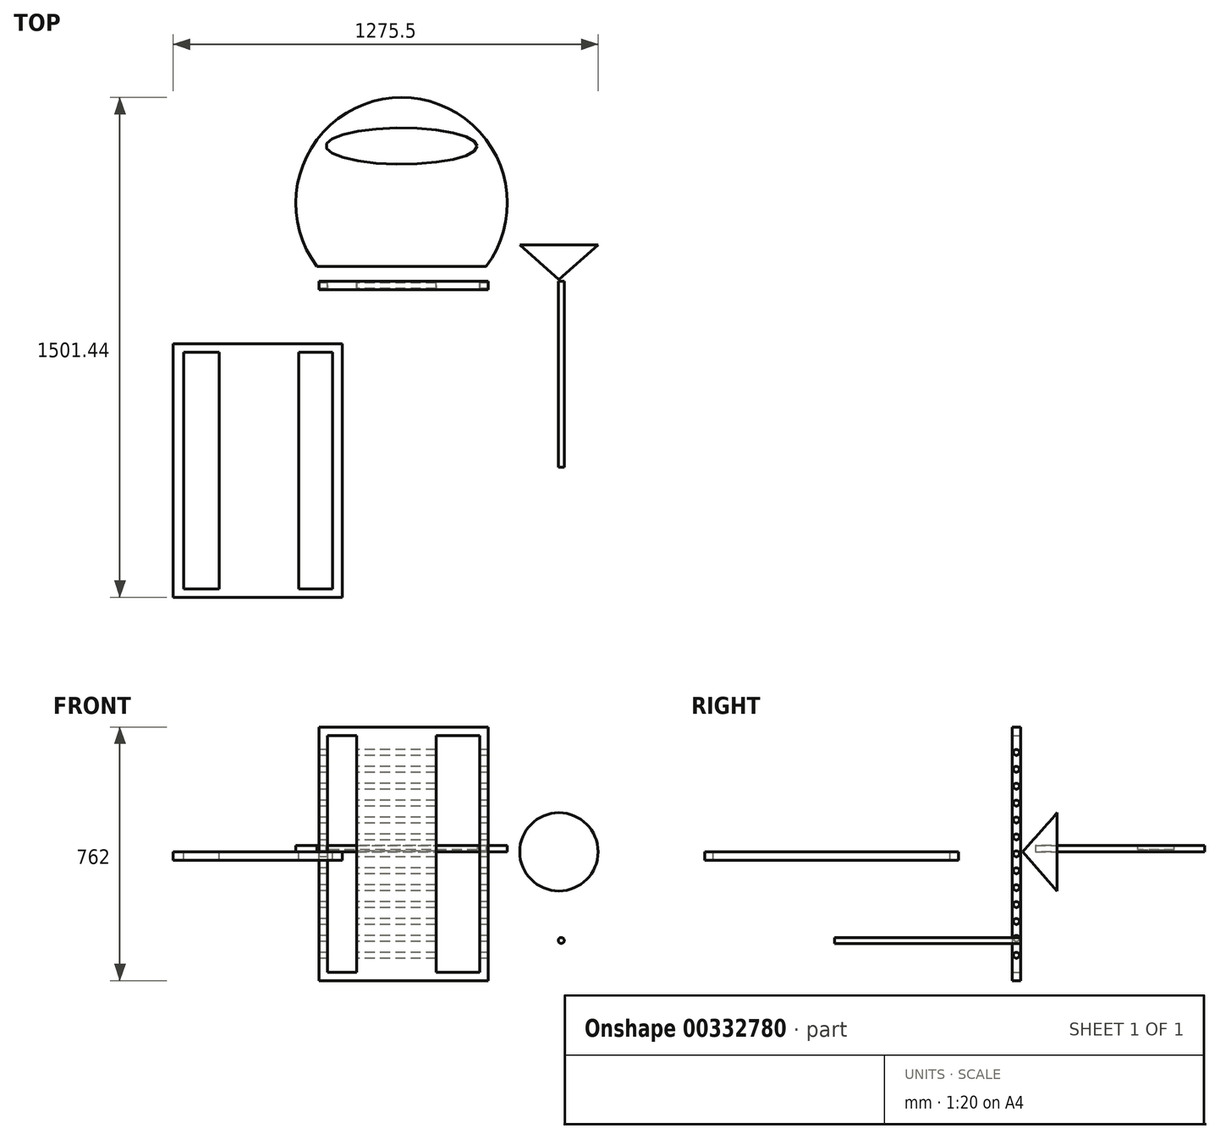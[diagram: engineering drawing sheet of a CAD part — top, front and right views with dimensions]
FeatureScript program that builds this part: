
annotation { "Feature Type Name" : "Feature", "Feature Type Description" : "" }
export const myFeature = defineFeature(function(context is Context, id is Id, definition is map)
    precondition{}
    {
        {
            var Q0;
            Q0=qCreatedBy(makeId("Front.planeOp"),FACE);
            var sketch = newSketch(context, id + "F0", { "sketchPlane" : qUnion([Q0])});
            skLineSegment(sketch, "E0", {"start": v(-402.52, -386.82) * mm, "end": v(-402.52, 375.18) * mm});
            skLineSegment(sketch, "E1", {"start": v(-402.52, 375.18) * mm, "end": v(105.48, 375.18) * mm});
            skLineSegment(sketch, "E2", {"start": v(105.48, 375.18) * mm, "end": v(105.48, -386.82) * mm});
            skLineSegment(sketch, "E3", {"start": v(105.48, -386.82) * mm, "end": v(-402.52, -386.82) * mm});
            skLineSegment(sketch, "E4", {"start": v(80.05, 349.78) * mm, "end": v(-51.74, 349.78) * mm});
            skLineSegment(sketch, "E5", {"start": v(-51.74, 349.78) * mm, "end": v(-51.74, -361.42) * mm});
            skLineSegment(sketch, "E6", {"start": v(-51.74, -361.42) * mm, "end": v(80.05, -361.42) * mm});
            skLineSegment(sketch, "E7", {"start": v(80.05, -361.42) * mm, "end": v(80.05, 349.78) * mm});
            skLineSegment(sketch, "E8", {"start": v(-51.74, 349.78) * mm, "end": v(-51.74, 375.18) * mm});
            skLineSegment(sketch, "E9", {"start": v(80.05, -361.42) * mm, "end": v(80.05, -386.82) * mm});
            skLineSegment(sketch, "E10", {"start": v(-290, 349.78) * mm, "end": v(-378.17, 349.78) * mm});
            skLineSegment(sketch, "E11", {"start": v(-378.17, 349.78) * mm, "end": v(-378.17, -361.42) * mm});
            skLineSegment(sketch, "E12", {"start": v(-378.17, -361.42) * mm, "end": v(-290, -361.42) * mm});
            skLineSegment(sketch, "E13", {"start": v(-290, -361.42) * mm, "end": v(-290, 349.78) * mm});
            skLineSegment(sketch, "E14", {"start": v(-290, -361.42) * mm, "end": v(-51.74, -361.42) * mm});
            skSolve(sketch);
        }
        {
            var Q0;
            Q0 = qSketchRegion(id + "F0", true);
            extrude(context, id + "F1", {"entities" : qUnion([Q0]), "depth" : 25.4 * mm});
        }
        {
            var Q0;
            Q0=qCreatedBy(makeId("Top.planeOp"),FACE);
            var sketch = newSketch(context, id + "F2", { "sketchPlane" : qUnion([Q0])});
            skLineSegment(sketch, "E15", {"start": v(-409.2, 44.16) * mm, "end": v(98.8, 44.16) * mm});
            skArc(sketch, "E16", {"start": v(98.8, 44.16) * mm, "mid": v(-155.2, 552.16) * mm, "end": v(-409.2, 44.16) * mm});
            skLineSegment(sketch, "E17", {"start": v(-155.2, 44.16) * mm, "end": v(-155.2, 552.16) * mm});
            skEllipse(sketch, "E18", {"center": v(-155.2, 406.06) * mm, "majorRadius": 226.76 * mm, "minorRadius": 54.56 * mm, "majorAxis": v(1, 0)});
            skSolve(sketch);
        }
        {
            var Q0;
            Q0 = qSketchRegion(id + "F2", true);
            extrude(context, id + "F3", {"entities" : qUnion([Q0]), "depth" : 19.05 * mm});
        }
        {
            var Q0;
            Q0=makeQuery(id+"F1.opExtrude","SWEPT_FACE",FACE,{"disambiguationData":[OSD([sQuery(id+"F0.wireOp",EDGE,"E0")])]});
            var sketch = newSketch(context, id + "F4", { "sketchPlane" : qUnion([Q0])});
            skCircle(sketch, "E19", {"center": v(13.05, -209.02) * mm, "radius": 8.9 * mm});
            skCircle(sketch, "E20", {"center": v(13.05, -259.82) * mm, "radius": 8.9 * mm});
            skCircle(sketch, "E21", {"center": v(13.05, -310.62) * mm, "radius": 8.9 * mm});
            skLineSegment(sketch, "E22", {"start": v(12.7, 375.18) * mm, "end": v(12.7, 349.78) * mm});
            skCircle(sketch, "E23", {"center": v(13.05, 298.98) * mm, "radius": 8.9 * mm});
            skCircle(sketch, "E24", {"center": v(13.4, 248.18) * mm, "radius": 8.9 * mm});
            skCircle(sketch, "E25", {"center": v(13.05, 197.38) * mm, "radius": 8.9 * mm});
            skCircle(sketch, "E26", {"center": v(13.05, 146.58) * mm, "radius": 8.9 * mm});
            skCircle(sketch, "E27", {"center": v(13.05, 95.78) * mm, "radius": 8.9 * mm});
            skCircle(sketch, "E28", {"center": v(13.05, 44.98) * mm, "radius": 8.9 * mm});
            skCircle(sketch, "E29", {"center": v(13.05, -5.82) * mm, "radius": 8.9 * mm});
            skCircle(sketch, "E30", {"center": v(13.05, -56.62) * mm, "radius": 8.9 * mm});
            skCircle(sketch, "E31", {"center": v(13.05, -107.42) * mm, "radius": 8.9 * mm});
            skCircle(sketch, "E32", {"center": v(13.05, -158.22) * mm, "radius": 8.9 * mm});
            skSolve(sketch);
        }
        {
            var Q0;
            Q0=makeQuery(id+"F4.imprint","IMPRINT",FACE,{"disambiguationData":[TD([[makeQuery(id+"F4.imprint","IMPRINT",EDGE,{"derivedFrom":sQuery(id+"F4.wireOp",EDGE,"KxLmF3Gb-bGkB-ipw0-DFv5-bGDR9Zjm1ckT")}),1.0]])]});
            var Q1;
            Q1=makeQuery(id+"F4.imprint","IMPRINT",FACE,{"disambiguationData":[TD([[makeQuery(id+"F4.imprint","IMPRINT",EDGE,{"derivedFrom":sQuery(id+"F4.wireOp",EDGE,"E21")}),1.0]])]});
            var Q2;
            Q2=makeQuery(id+"F4.imprint","IMPRINT",FACE,{"disambiguationData":[TD([[makeQuery(id+"F4.imprint","IMPRINT",EDGE,{"derivedFrom":sQuery(id+"F4.wireOp",EDGE,"E20")}),1.0]])]});
            var Q3;
            Q3=makeQuery(id+"F4.imprint","IMPRINT",FACE,{"disambiguationData":[TD([[makeQuery(id+"F4.imprint","IMPRINT",EDGE,{"derivedFrom":sQuery(id+"F4.wireOp",EDGE,"E19")}),1.0]])]});
            var Q4;
            Q4=makeQuery(id+"F4.imprint","IMPRINT",FACE,{"disambiguationData":[TD([[makeQuery(id+"F4.imprint","IMPRINT",EDGE,{"derivedFrom":sQuery(id+"F4.wireOp",EDGE,"SBUI3A1f-vfDp-xBPE-MnOG-4KJ5W3Gntg9e")}),1.0]])]});
            var Q5;
            Q5=makeQuery(id+"F4.imprint","IMPRINT",FACE,{"disambiguationData":[TD([[makeQuery(id+"F4.imprint","IMPRINT",EDGE,{"derivedFrom":sQuery(id+"F4.wireOp",EDGE,"ilClZEr1-WkWB-SVEu-xgAh-d21V4UNr9qtg")}),1.0]])]});
            var Q6;
            Q6=makeQuery(id+"F4.imprint","IMPRINT",FACE,{"disambiguationData":[TD([[makeQuery(id+"F4.imprint","IMPRINT",EDGE,{"derivedFrom":sQuery(id+"F4.wireOp",EDGE,"wnZTXNVM-36Ts-yCiN-EnVW-6zEoZN5PAqgz")}),1.0]])]});
            var Q7;
            Q7=makeQuery(id+"F4.imprint","IMPRINT",FACE,{"disambiguationData":[TD([[makeQuery(id+"F4.imprint","IMPRINT",EDGE,{"derivedFrom":sQuery(id+"F4.wireOp",EDGE,"8CFQUjnE-zp7q-roIU-KdL1-6CvUVFCRa30A")}),1.0]])]});
            var Q8;
            Q8=makeQuery(id+"F4.imprint","IMPRINT",FACE,{"disambiguationData":[TD([[makeQuery(id+"F4.imprint","IMPRINT",EDGE,{"derivedFrom":sQuery(id+"F4.wireOp",EDGE,"dk1FrOmF-X76H-YBRf-a3w2-1DeCIXSDKJ0s")}),1.0]])]});
            var Q9;
            Q9=makeQuery(id+"F4.imprint","IMPRINT",FACE,{"disambiguationData":[TD([[makeQuery(id+"F4.imprint","IMPRINT",EDGE,{"derivedFrom":sQuery(id+"F4.wireOp",EDGE,"kuolFWdS-myks-ns8r-KsmL-CEO9Fm7HA733")}),1.0]])]});
            var Q10;
            Q10=makeQuery(id+"F4.imprint","IMPRINT",FACE,{"disambiguationData":[TD([[makeQuery(id+"F4.imprint","IMPRINT",EDGE,{"derivedFrom":sQuery(id+"F4.wireOp",EDGE,"JJCqWmZP-dY7G-QudE-gpbD-zNKJ9OVh3fGP")}),1.0]])]});
            var Q11;
            Q11=makeQuery(id+"F4.imprint","IMPRINT",FACE,{"disambiguationData":[TD([[makeQuery(id+"F4.imprint","IMPRINT",EDGE,{"derivedFrom":sQuery(id+"F4.wireOp",EDGE,"UWQk5Cos-suA6-4IC4-ZAEo-IQIC4gf6qBqO")}),1.0]])]});
            var Q12;
            Q12=makeQuery(id+"F4.imprint","IMPRINT",FACE,{"disambiguationData":[TD([[makeQuery(id+"F4.imprint","IMPRINT",EDGE,{"derivedFrom":sQuery(id+"F4.wireOp",EDGE,"E2on6uqV-6kPG-ftVK-5GpS-Gi3AbfQCoDi4")}),1.0]])]});
            var Q13;
            Q13=makeQuery(id+"F4.imprint","IMPRINT",FACE,{"disambiguationData":[TD([[makeQuery(id+"F4.imprint","IMPRINT",EDGE,{"derivedFrom":sQuery(id+"F4.wireOp",EDGE,"fvvu0ycN-TSmg-J3CF-A7jG-3QvBUFncVqg9")}),1.0]])]});
            var Q14;
            Q14=makeQuery(id+"F4.imprint","IMPRINT",FACE,{"disambiguationData":[TD([[makeQuery(id+"F4.imprint","IMPRINT",EDGE,{"derivedFrom":sQuery(id+"F4.wireOp",EDGE,"if6vlhrL-GMo5-v6cd-j6Fg-0aG144yE2SJh")}),1.0]])]});
            var Q15;
            Q15=makeQuery(id+"F4.imprint","IMPRINT",FACE,{"disambiguationData":[TD([[makeQuery(id+"F4.imprint","IMPRINT",EDGE,{"derivedFrom":sQuery(id+"F4.wireOp",EDGE,"E26")}),1.0]])]});
            var Q16;
            Q16=makeQuery(id+"F4.imprint","IMPRINT",FACE,{"disambiguationData":[TD([[makeQuery(id+"F4.imprint","IMPRINT",EDGE,{"derivedFrom":sQuery(id+"F4.wireOp",EDGE,"E27")}),1.0]])]});
            var Q17;
            Q17=makeQuery(id+"F4.imprint","IMPRINT",FACE,{"disambiguationData":[TD([[makeQuery(id+"F4.imprint","IMPRINT",EDGE,{"derivedFrom":sQuery(id+"F4.wireOp",EDGE,"E28")}),1.0]])]});
            var Q18;
            Q18=makeQuery(id+"F4.imprint","IMPRINT",FACE,{"disambiguationData":[TD([[makeQuery(id+"F4.imprint","IMPRINT",EDGE,{"derivedFrom":sQuery(id+"F4.wireOp",EDGE,"E29")}),1.0]])]});
            var Q19;
            Q19=makeQuery(id+"F4.imprint","IMPRINT",FACE,{"disambiguationData":[TD([[makeQuery(id+"F4.imprint","IMPRINT",EDGE,{"derivedFrom":sQuery(id+"F4.wireOp",EDGE,"E30")}),1.0]])]});
            var Q20;
            Q20=makeQuery(id+"F4.imprint","IMPRINT",FACE,{"disambiguationData":[TD([[makeQuery(id+"F4.imprint","IMPRINT",EDGE,{"derivedFrom":sQuery(id+"F4.wireOp",EDGE,"E31")}),1.0]])]});
            var Q21;
            Q21=makeQuery(id+"F4.imprint","IMPRINT",FACE,{"disambiguationData":[TD([[makeQuery(id+"F4.imprint","IMPRINT",EDGE,{"derivedFrom":sQuery(id+"F4.wireOp",EDGE,"E32")}),1.0]])]});
            var Q22;
            Q22=makeQuery(id+"F4.imprint","IMPRINT",FACE,{"disambiguationData":[TD([[makeQuery(id+"F4.imprint","IMPRINT",EDGE,{"derivedFrom":sQuery(id+"F4.wireOp",EDGE,"E23")}),1.0]])]});
            var Q23;
            Q23=makeQuery(id+"F4.imprint","IMPRINT",FACE,{"disambiguationData":[TD([[makeQuery(id+"F4.imprint","IMPRINT",EDGE,{"derivedFrom":sQuery(id+"F4.wireOp",EDGE,"E24")}),1.0]])]});
            var Q24;
            Q24=makeQuery(id+"F4.imprint","IMPRINT",FACE,{"disambiguationData":[TD([[makeQuery(id+"F4.imprint","IMPRINT",EDGE,{"derivedFrom":sQuery(id+"F4.wireOp",EDGE,"E25")}),1.0]])]});
            extrude(context, id + "F5", {"entities" : qUnion([Q0, Q1, Q2, Q3, Q4, Q5, Q6, Q7, Q8, Q9, Q10, Q11, Q12, Q13, Q14, Q15, Q16, Q17, Q18, Q19, Q20, Q21, Q22, Q23, Q24]), "operationType" : NewBodyOperationType.REMOVE, "endBound" : BoundingType.THROUGH_ALL, "oppositeDirection" : true, "depth" : 25.4 * mm});
        }
        {
            var Q0;
            Q0=qCreatedBy(makeId("Top.planeOp"),FACE);
            var sketch = newSketch(context, id + "F6", { "sketchPlane" : qUnion([Q0])});
            skLineSegment(sketch, "E33", {"start": v(199.63, 109.45) * mm, "end": v(317.2, 5.52) * mm});
            skLineSegment(sketch, "E34", {"start": v(199.63, 109.45) * mm, "end": v(317.2, 109.45) * mm});
            skLineSegment(sketch, "E35", {"start": v(317.2, 109.45) * mm, "end": v(317.2, 5.52) * mm});
            skSolve(sketch);
        }
        {
            var Q0;
            Q0=makeQuery(id+"F6.imprint","IMPRINT",FACE,{"disambiguationData":[TD([[makeQuery(id+"F6.imprint","IMPRINT",EDGE,{"derivedFrom":sQuery(id+"F6.wireOp",EDGE,"E33")}),1.0]])]});
            var Q1;
            Q1=sQuery(id+"F6.wireOp",EDGE,"E35");
            revolve(context, id + "F7", {"entities" : qUnion([Q0]), "axis" : qUnion([Q1]), "revolveType" : RevolveType.FULL});
        }
        {
            var Q0;
            Q0=qCreatedBy(makeId("Front.planeOp"),FACE);
            var sketch = newSketch(context, id + "F8", { "sketchPlane" : qUnion([Q0])});
            skCircle(sketch, "E36", {"center": v(324.3, -266.21) * mm, "radius": 8.9 * mm});
            skSolve(sketch);
        }
        {
            var Q0;
            Q0=makeQuery(id+"F8.imprint","IMPRINT",FACE,{"disambiguationData":[TD([[makeQuery(id+"F8.imprint","IMPRINT",EDGE,{"derivedFrom":sQuery(id+"F8.wireOp",EDGE,"E36")}),1.0]])]});
            extrude(context, id + "F9", {"entities" : qUnion([Q0]), "depth" : 558.8 * mm});
        }
        {
            var Q0;
            Q0=qCreatedBy(makeId("Top.planeOp"),FACE);
            var sketch = newSketch(context, id + "F10", { "sketchPlane" : qUnion([Q0])});
            skLineSegment(sketch, "E37", {"start": v(-840.72, -187.28) * mm, "end": v(-840.72, -949.28) * mm});
            skLineSegment(sketch, "E38", {"start": v(-840.72, -949.28) * mm, "end": v(-332.72, -949.28) * mm});
            skLineSegment(sketch, "E39", {"start": v(-332.72, -949.28) * mm, "end": v(-332.72, -187.28) * mm});
            skLineSegment(sketch, "E40", {"start": v(-332.72, -187.28) * mm, "end": v(-840.72, -187.28) * mm});
            skLineSegment(sketch, "E41", {"start": v(-754.8, -187.28) * mm, "end": v(-754.8, -212.68) * mm});
            skPoint(sketch, "E42.start.orphan", {"position": v(-709.42, -260.3) * mm});
            skLineSegment(sketch, "E43", {"start": v(-809.48, -212.68) * mm, "end": v(-702.6, -212.68) * mm});
            skLineSegment(sketch, "E44", {"start": v(-702.6, -212.68) * mm, "end": v(-702.6, -923.88) * mm});
            skLineSegment(sketch, "E45", {"start": v(-809.48, -212.68) * mm, "end": v(-809.48, -923.88) * mm});
            skLineSegment(sketch, "E46", {"start": v(-809.48, -923.88) * mm, "end": v(-702.6, -923.88) * mm});
            skLineSegment(sketch, "E47", {"start": v(-426.68, -187.28) * mm, "end": v(-426.68, -212.68) * mm});
            skLineSegment(sketch, "E48", {"start": v(-464.34, -212.68) * mm, "end": v(-362.74, -212.68) * mm});
            skLineSegment(sketch, "E49", {"start": v(-362.74, -212.68) * mm, "end": v(-362.74, -923.88) * mm});
            skLineSegment(sketch, "E50", {"start": v(-362.74, -923.88) * mm, "end": v(-464.34, -923.88) * mm});
            skLineSegment(sketch, "E51", {"start": v(-464.34, -923.88) * mm, "end": v(-464.34, -212.68) * mm});
            skLineSegment(sketch, "E52", {"start": v(-702.6, -212.68) * mm, "end": v(-464.34, -212.68) * mm});
            skSolve(sketch);
        }
        {
            var Q0;
            Q0 = qSketchRegion(id + "F10", true);
            extrude(context, id + "F11", {"entities" : qUnion([Q0]), "oppositeDirection" : true, "depth" : 25.4 * mm});
        }
        {
            var Q0;
            {var subQ0=sQuery(id+"F2.wireOp",EDGE,"E18");var subQ1=sQuery(id+"F2.wireOp",EDGE,"E17");var subQ2=makeQuery(id+"F2.imprint","INTERSECT",VERTEX,{"disambiguationData":[OD(0.0)],"derivedFrom":[subQ1,subQ0]});Q0=makeQuery(id+"F2.imprint","IMPRINT",FACE,{"disambiguationData":[TD([[makeQuery(id+"F2.imprint","IMPRINT",EDGE,{"disambiguationData":[TD([[subQ2,-1.0]])],"derivedFrom":subQ1}),1.0]])]});}
            var Q1;
            {var subQ0=sQuery(id+"F2.wireOp",EDGE,"E18");var subQ1=sQuery(id+"F2.wireOp",EDGE,"E17");var subQ2=makeQuery(id+"F2.imprint","INTERSECT",VERTEX,{"disambiguationData":[OD(0.0)],"derivedFrom":[subQ1,subQ0]});Q1=makeQuery(id+"F2.imprint","IMPRINT",FACE,{"disambiguationData":[TD([[makeQuery(id+"F2.imprint","IMPRINT",EDGE,{"disambiguationData":[TD([[subQ2,-1.0]])],"derivedFrom":subQ1}),-1.0]])]});}
            extrude(context, id + "F12", {"entities" : qUnion([Q0, Q1]), "operationType" : NewBodyOperationType.ADD, "depth" : 6.35 * mm});
        }
    });
